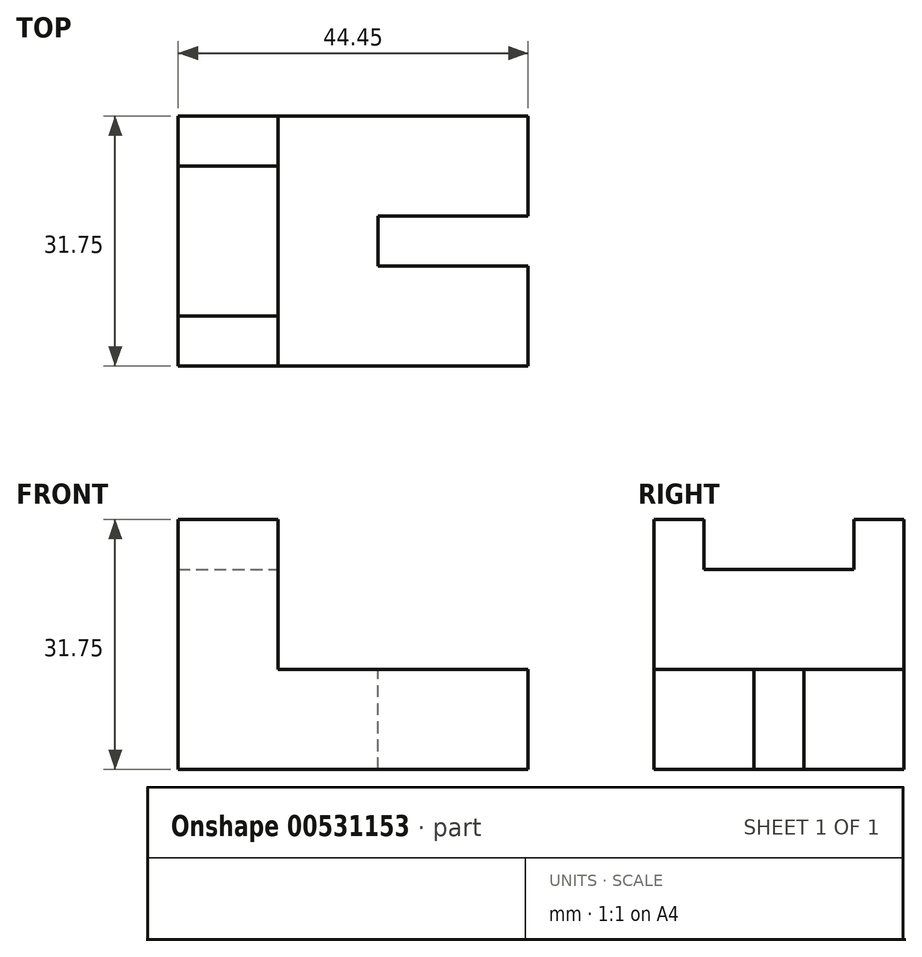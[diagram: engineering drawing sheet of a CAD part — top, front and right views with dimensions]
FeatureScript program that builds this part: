
annotation { "Feature Type Name" : "Feature", "Feature Type Description" : "" }
export const myFeature = defineFeature(function(context is Context, id is Id, definition is map)
    precondition{}
    {
        {
            var Q0;
            Q0=qCreatedBy(makeId("Top.planeOp"),FACE);
            var sketch = newSketch(context, id + "F0", { "sketchPlane" : qUnion([Q0])});
            skLineSegment(sketch, "E0.bottom", {"start": v(0, 0) * mm, "end": v(44.45, 0) * mm});
            skLineSegment(sketch, "E0.top", {"start": v(0, 31.75) * mm, "end": v(44.45, 31.75) * mm});
            skLineSegment(sketch, "E0.left", {"start": v(0, 0) * mm, "end": v(0, 31.75) * mm});
            skLineSegment(sketch, "E0.right", {"start": v(44.45, 0) * mm, "end": v(44.45, 31.75) * mm});
            skSolve(sketch);
        }
        {
            var Q0;
            Q0=makeQuery(id+"F0.imprint","IMPRINT",FACE,{"disambiguationData":[TD([[makeQuery(id+"F0.imprint","IMPRINT",EDGE,{"derivedFrom":sQuery(id+"F0.wireOp",EDGE,"E0.bottom")}),1.0]])]});
            extrude(context, id + "F1", {"entities" : qUnion([Q0]), "depth" : 31.75 * mm, "offsetDistance" : 25.4 * mm});
        }
        {
            var Q0;
            Q0=makeQuery(id+"F1.opExtrude","SWEPT_FACE",FACE,{"disambiguationData":[OSD([sQuery(id+"F0.wireOp",EDGE,"E0.bottom")])]});
            var sketch = newSketch(context, id + "F2", { "sketchPlane" : qUnion([Q0])});
            skLineSegment(sketch, "E1.bottom", {"start": v(44.45, 31.75) * mm, "end": v(12.7, 31.75) * mm});
            skLineSegment(sketch, "E1.top", {"start": v(44.45, 12.7) * mm, "end": v(12.7, 12.7) * mm});
            skLineSegment(sketch, "E1.left", {"start": v(44.45, 31.75) * mm, "end": v(44.45, 12.7) * mm});
            skLineSegment(sketch, "E1.right", {"start": v(12.7, 31.75) * mm, "end": v(12.7, 12.7) * mm});
            skSolve(sketch);
        }
        {
            var Q0;
            Q0=makeQuery(id+"F2.imprint","IMPRINT",FACE,{"disambiguationData":[TD([[makeQuery(id+"F2.imprint","IMPRINT",EDGE,{"derivedFrom":sQuery(id+"F2.wireOp",EDGE,"E1.bottom")}),-1.0]])]});
            extrude(context, id + "F3", {"entities" : qUnion([Q0]), "operationType" : NewBodyOperationType.REMOVE, "endBound" : BoundingType.THROUGH_ALL, "oppositeDirection" : true, "depth" : 25.4 * mm, "offsetDistance" : 25.4 * mm});
        }
        {
            var Q0;
            Q0=makeQuery(id+"F1.opExtrude","SWEPT_FACE",FACE,{"disambiguationData":[OSD([sQuery(id+"F0.wireOp",EDGE,"E0.right")])]});
            var sketch = newSketch(context, id + "F4", { "sketchPlane" : qUnion([Q0])});
            skLineSegment(sketch, "E2.bottom", {"start": v(0, 0) * mm, "end": v(12.7, 0) * mm, "construction": true});
            skLineSegment(sketch, "E2.top", {"start": v(0, 12.7) * mm, "end": v(12.7, 12.7) * mm, "construction": true});
            skLineSegment(sketch, "E2.left", {"start": v(0, 0) * mm, "end": v(0, 12.7) * mm, "construction": true});
            skLineSegment(sketch, "E2.right", {"start": v(12.7, 0) * mm, "end": v(12.7, 12.7) * mm, "construction": true});
            skLineSegment(sketch, "E3.bottom", {"start": v(12.7, 0) * mm, "end": v(19.05, 0) * mm});
            skLineSegment(sketch, "E3.top", {"start": v(12.7, 12.7) * mm, "end": v(19.05, 12.7) * mm});
            skLineSegment(sketch, "E3.left", {"start": v(12.7, 0) * mm, "end": v(12.7, 12.7) * mm});
            skLineSegment(sketch, "E3.right", {"start": v(19.05, 0) * mm, "end": v(19.05, 12.7) * mm});
            skSolve(sketch);
        }
        {
            var Q0;
            Q0=makeQuery(id+"F4.imprint","IMPRINT",FACE,{"disambiguationData":[TD([[makeQuery(id+"F4.imprint","IMPRINT",EDGE,{"derivedFrom":sQuery(id+"F4.wireOp",EDGE,"E3.bottom")}),1.0]])]});
            extrude(context, id + "F5", {"entities" : qUnion([Q0]), "operationType" : NewBodyOperationType.REMOVE, "oppositeDirection" : true, "depth" : 19.05 * mm, "offsetDistance" : 25.4 * mm});
        }
        {
            var Q0;
            Q0=makeQuery(id+"F1.opExtrude","CAP_FACE",FACE,{"disambiguationData":[OSD([sQuery(id+"F0.wireOp",EDGE,"E0.bottom"),sQuery(id+"F0.wireOp",EDGE,"E0.top"),sQuery(id+"F0.wireOp",EDGE,"E0.left"),sQuery(id+"F0.wireOp",EDGE,"E0.right")])],"isStart":false});
            var sketch = newSketch(context, id + "F6", { "sketchPlane" : qUnion([Q0])});
            skLineSegment(sketch, "E4.bottom", {"start": v(0, 31.75) * mm, "end": v(12.7, 31.75) * mm, "construction": true});
            skLineSegment(sketch, "E4.top", {"start": v(0, 25.4) * mm, "end": v(12.7, 25.4) * mm, "construction": true});
            skLineSegment(sketch, "E4.left", {"start": v(0, 31.75) * mm, "end": v(0, 25.4) * mm, "construction": true});
            skLineSegment(sketch, "E4.right", {"start": v(12.7, 31.75) * mm, "end": v(12.7, 25.4) * mm, "construction": true});
            skLineSegment(sketch, "E5.bottom", {"start": v(0, 25.4) * mm, "end": v(12.7, 25.4) * mm});
            skLineSegment(sketch, "E5.top", {"start": v(0, 6.35) * mm, "end": v(12.7, 6.35) * mm});
            skLineSegment(sketch, "E5.left", {"start": v(0, 25.4) * mm, "end": v(0, 6.35) * mm});
            skLineSegment(sketch, "E5.right", {"start": v(12.7, 25.4) * mm, "end": v(12.7, 6.35) * mm});
            skSolve(sketch);
        }
        {
            var Q0;
            Q0=makeQuery(id+"F6.imprint","IMPRINT",FACE,{"disambiguationData":[TD([[makeQuery(id+"F6.imprint","IMPRINT",EDGE,{"derivedFrom":sQuery(id+"F6.wireOp",EDGE,"E5.bottom")}),-1.0]])]});
            extrude(context, id + "F7", {"entities" : qUnion([Q0]), "operationType" : NewBodyOperationType.REMOVE, "oppositeDirection" : true, "depth" : 6.35 * mm, "offsetDistance" : 25.4 * mm});
        }
    });
